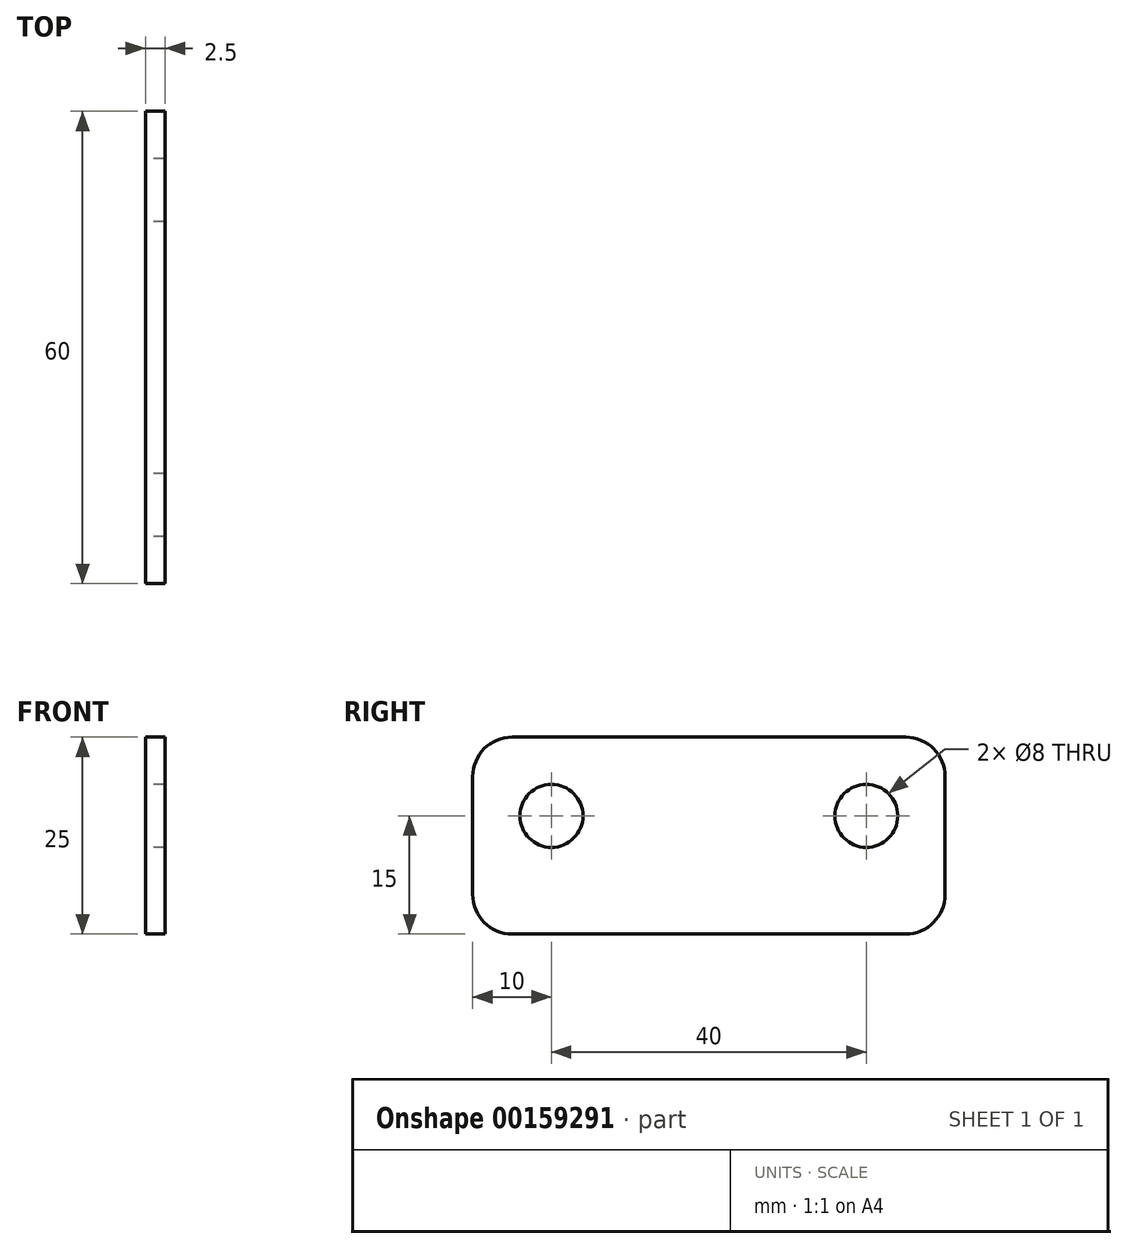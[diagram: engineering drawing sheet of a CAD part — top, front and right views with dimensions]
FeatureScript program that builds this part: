
annotation { "Feature Type Name" : "Feature", "Feature Type Description" : "" }
export const myFeature = defineFeature(function(context is Context, id is Id, definition is map)
    precondition{}
    {
        {
            var Q0;
            Q0=qCreatedBy(makeId("Right.planeOp"),FACE);
            var sketch = newSketch(context, id + "F0", { "sketchPlane" : qUnion([Q0])});
            skLineSegment(sketch, "E0.bottom", {"start": v(5, 0) * mm, "end": v(55, 0) * mm});
            skLineSegment(sketch, "E0.top", {"start": v(5, -25) * mm, "end": v(55, -25) * mm});
            skLineSegment(sketch, "E0.left", {"start": v(0, -5) * mm, "end": v(0, -20) * mm});
            skLineSegment(sketch, "E0.right", {"start": v(60, -5) * mm, "end": v(60, -20) * mm});
            skPoint(sketch, "E1.visualSharp", {"position": v(0, 0) * mm});
            skArc(sketch, "E1.filletArc", {"start": v(5, 0) * mm, "mid": v(1.46, -1.46) * mm, "end": v(0, -5) * mm});
            skPoint(sketch, "E2.visualSharp", {"position": v(0, -25) * mm});
            skArc(sketch, "E2.filletArc", {"start": v(0, -20) * mm, "mid": v(1.46, -23.54) * mm, "end": v(5, -25) * mm});
            skPoint(sketch, "E3.visualSharp", {"position": v(60, -25) * mm});
            skArc(sketch, "E3.filletArc", {"start": v(55, -25) * mm, "mid": v(58.54, -23.54) * mm, "end": v(60, -20) * mm});
            skPoint(sketch, "E4.visualSharp", {"position": v(60, 0) * mm});
            skArc(sketch, "E4.filletArc", {"start": v(60, -5) * mm, "mid": v(58.54, -1.46) * mm, "end": v(55, 0) * mm});
            skCircle(sketch, "E5", {"center": v(10, -10) * mm, "radius": 4 * mm});
            skCircle(sketch, "E6", {"center": v(50, -10) * mm, "radius": 4 * mm});
            skSolve(sketch);
        }
        {
            var Q0;
            Q0=makeQuery(id+"F0.imprint","IMPRINT",FACE,{"disambiguationData":[TD([[makeQuery(id+"F0.imprint","IMPRINT",EDGE,{"derivedFrom":sQuery(id+"F0.wireOp",EDGE,"E0.bottom")}),-1.0]])]});
            extrude(context, id + "F1", {"entities" : qUnion([Q0]), "depth" : 2.5 * mm});
        }
    });
